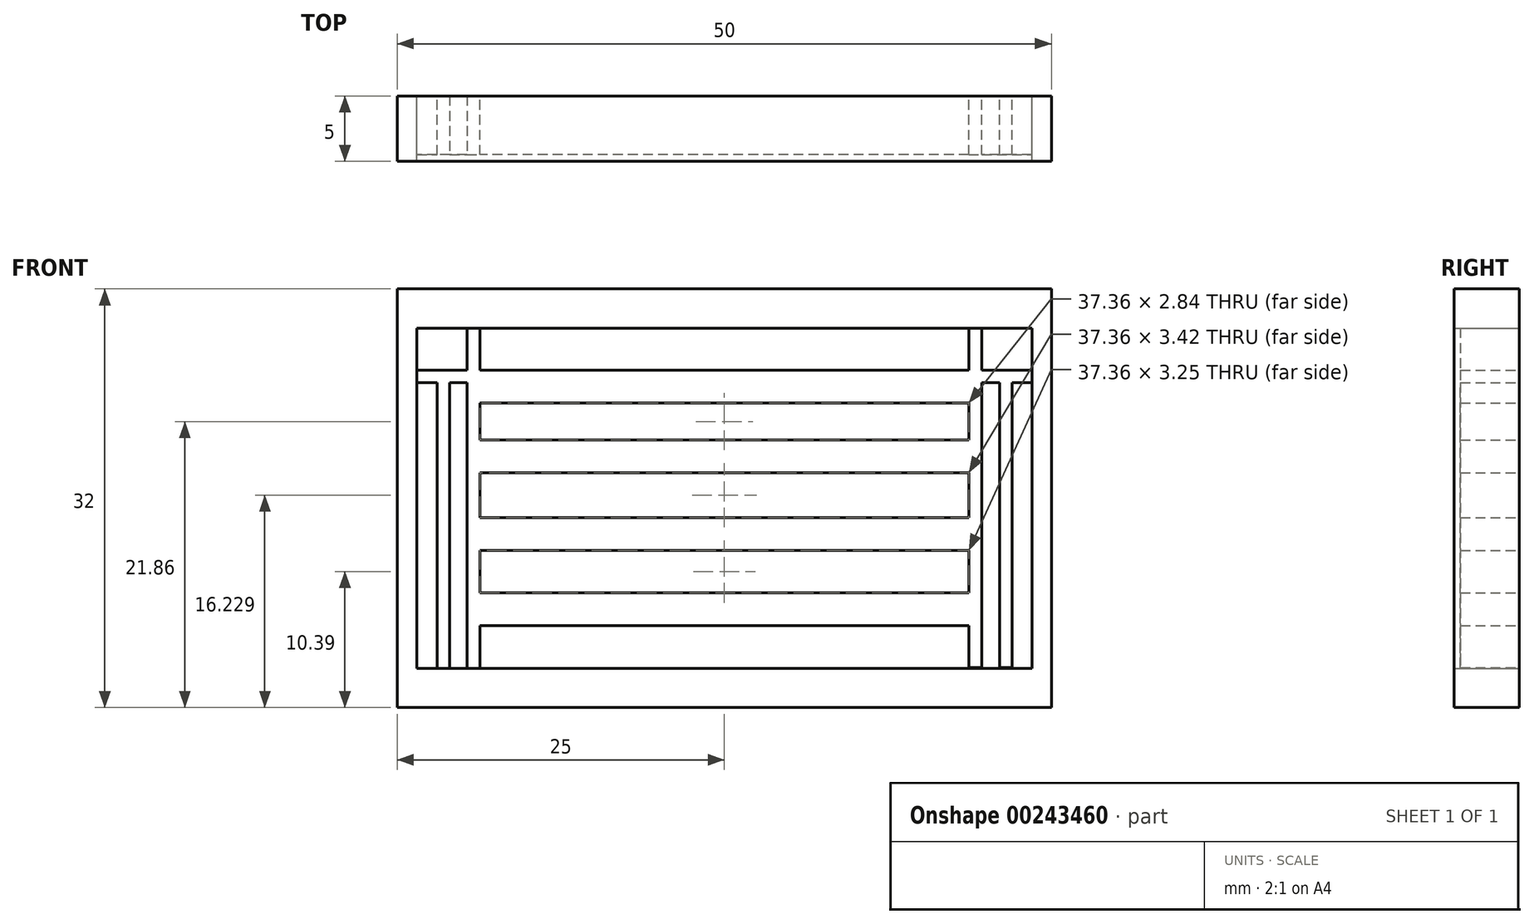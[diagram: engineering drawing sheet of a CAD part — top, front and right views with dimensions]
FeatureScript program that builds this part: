
annotation { "Feature Type Name" : "Feature", "Feature Type Description" : "" }
export const myFeature = defineFeature(function(context is Context, id is Id, definition is map)
    precondition{}
    {
        {
            var Q0;
            Q0=qCreatedBy(makeId("Front.planeOp"),FACE);
            var sketch = newSketch(context, id + "F0", { "sketchPlane" : qUnion([Q0])});
            skLineSegment(sketch, "E0", {"start": v(0, 0) * mm, "end": v(50, 0) * mm});
            skLineSegment(sketch, "E1", {"start": v(50, 0) * mm, "end": v(50, 32) * mm});
            skLineSegment(sketch, "E2", {"start": v(50, 32) * mm, "end": v(0, 32) * mm});
            skLineSegment(sketch, "E3", {"start": v(0, 32) * mm, "end": v(0, 0) * mm});
            skLineSegment(sketch, "E4", {"start": v(1.5, 29) * mm, "end": v(48.5, 29) * mm});
            skLineSegment(sketch, "E5", {"start": v(48.5, 29) * mm, "end": v(48.5, 3) * mm});
            skLineSegment(sketch, "E6", {"start": v(48.5, 3) * mm, "end": v(1.5, 3) * mm});
            skLineSegment(sketch, "E7", {"start": v(1.5, 3) * mm, "end": v(1.5, 29) * mm});
            skLineSegment(sketch, "E8", {"start": v(8, 29) * mm, "end": v(8, 3) * mm});
            skLineSegment(sketch, "E9", {"start": v(8, 3) * mm, "end": v(6.8, 3) * mm});
            skLineSegment(sketch, "E10", {"start": v(6.8, 3) * mm, "end": v(6.8, 29) * mm});
            skLineSegment(sketch, "E11", {"start": v(6.8, 29) * mm, "end": v(8, 29) * mm});
            skLineSegment(sketch, "E12", {"start": v(6.8, 26.52) * mm, "end": v(1.5, 26.52) * mm});
            skLineSegment(sketch, "E13", {"start": v(1.5, 26.52) * mm, "end": v(1.5, 25.4) * mm});
            skLineSegment(sketch, "E14", {"start": v(1.5, 25.4) * mm, "end": v(6.8, 25.4) * mm});
            skLineSegment(sketch, "E15", {"start": v(6.8, 25.4) * mm, "end": v(6.8, 26.52) * mm});
            skLineSegment(sketch, "E16", {"start": v(4.75, 25.4) * mm, "end": v(4.75, 3) * mm});
            skLineSegment(sketch, "E17", {"start": v(4.75, 3) * mm, "end": v(3.81, 3) * mm});
            skLineSegment(sketch, "E18", {"start": v(3.81, 3) * mm, "end": v(3.81, 25.4) * mm});
            skLineSegment(sketch, "E19", {"start": v(3.81, 25.4) * mm, "end": v(4.75, 25.4) * mm});
            skSolve(sketch);
        }
        {
            var Q0;
            Q0 = qSketchRegion(id + "F0", true);
            extrude(context, id + "F1", {"entities" : qUnion([Q0]), "depth" : 5 * mm, "offsetDistance" : 25 * mm});
        }
        {
            var Q0;
            Q0=qCreatedBy(makeId("Front.planeOp"),FACE);
            var sketch = newSketch(context, id + "F2", { "sketchPlane" : qUnion([Q0])});
            skLineSegment(sketch, "E20", {"start": v(6.32, 29.03) * mm, "end": v(6.32, 2.97) * mm});
            skLineSegment(sketch, "E21", {"start": v(6.32, 2.97) * mm, "end": v(5.32, 2.97) * mm});
            skLineSegment(sketch, "E22", {"start": v(5.32, 2.97) * mm, "end": v(5.32, 29.03) * mm});
            skLineSegment(sketch, "E23", {"start": v(5.32, 29.03) * mm, "end": v(6.32, 29.03) * mm});
            skLineSegment(sketch, "E24", {"start": v(5.32, 25.78) * mm, "end": v(1.5, 25.78) * mm});
            skLineSegment(sketch, "E25", {"start": v(1.5, 25.78) * mm, "end": v(1.5, 24.83) * mm});
            skLineSegment(sketch, "E26", {"start": v(1.5, 24.83) * mm, "end": v(5.32, 24.83) * mm});
            skLineSegment(sketch, "E27", {"start": v(5.32, 24.83) * mm, "end": v(5.32, 25.78) * mm});
            skLineSegment(sketch, "E28", {"start": v(4, 24.83) * mm, "end": v(4, 2.97) * mm});
            skLineSegment(sketch, "E29", {"start": v(4, 2.97) * mm, "end": v(3.05, 2.97) * mm});
            skLineSegment(sketch, "E30", {"start": v(3.05, 2.97) * mm, "end": v(3.05, 24.83) * mm});
            skLineSegment(sketch, "E31", {"start": v(3.05, 24.83) * mm, "end": v(4, 24.83) * mm});
            skLineSegment(sketch, "E32", {"start": v(43.5, 29) * mm, "end": v(44.68, 29) * mm});
            skLineSegment(sketch, "E33", {"start": v(44.68, 29) * mm, "end": v(44.68, 3.05) * mm});
            skLineSegment(sketch, "E34", {"start": v(44.68, 3.05) * mm, "end": v(43.68, 3.05) * mm});
            skLineSegment(sketch, "E35", {"start": v(43.68, 3.05) * mm, "end": v(43.68, 29) * mm});
            skLineSegment(sketch, "E36", {"start": v(44.68, 25.78) * mm, "end": v(48.5, 25.78) * mm});
            skLineSegment(sketch, "E37", {"start": v(48.5, 25.78) * mm, "end": v(48.5, 24.83) * mm});
            skLineSegment(sketch, "E38", {"start": v(48.5, 24.83) * mm, "end": v(46.98, 24.83) * mm});
            skLineSegment(sketch, "E39", {"start": v(44.68, 24.83) * mm, "end": v(44.68, 25.78) * mm});
            skPoint(sketch, "E40.end.orphan", {"position": v(46.59, 24.83) * mm});
            skPoint(sketch, "E40.start.orphan", {"position": v(46.98, 24.83) * mm});
            skPoint(sketch, "E41.start.orphan", {"position": v(47.01, 3.05) * mm});
            skLineSegment(sketch, "E42", {"start": v(46.98, 24.83) * mm, "end": v(46.98, 3.05) * mm});
            skLineSegment(sketch, "E43", {"start": v(46.98, 3.05) * mm, "end": v(46.03, 3.05) * mm});
            skLineSegment(sketch, "E44", {"start": v(46.03, 3.05) * mm, "end": v(46.03, 24.83) * mm});
            skLineSegment(sketch, "E45", {"start": v(46.03, 24.83) * mm, "end": v(46.98, 24.83) * mm});
            skLineSegment(sketch, "E46.trimOffspring", {"start": v(46.59, 24.83) * mm, "end": v(44.68, 24.83) * mm});
            skLineSegment(sketch, "E47", {"start": v(6.32, 25.78) * mm, "end": v(43.68, 25.78) * mm});
            skLineSegment(sketch, "E48", {"start": v(43.68, 25.78) * mm, "end": v(43.68, 23.28) * mm});
            skLineSegment(sketch, "E49", {"start": v(43.68, 23.28) * mm, "end": v(6.32, 23.28) * mm});
            skLineSegment(sketch, "E50", {"start": v(6.32, 23.28) * mm, "end": v(6.32, 25.78) * mm});
            skLineSegment(sketch, "E51", {"start": v(6.32, 20.44) * mm, "end": v(43.68, 20.44) * mm});
            skLineSegment(sketch, "E52", {"start": v(43.68, 20.44) * mm, "end": v(43.68, 17.94) * mm});
            skLineSegment(sketch, "E53", {"start": v(43.68, 17.94) * mm, "end": v(6.32, 17.94) * mm});
            skLineSegment(sketch, "E54", {"start": v(6.32, 17.94) * mm, "end": v(6.32, 20.44) * mm});
            skLineSegment(sketch, "E55", {"start": v(6.32, 14.52) * mm, "end": v(43.68, 14.52) * mm});
            skLineSegment(sketch, "E56", {"start": v(43.68, 14.52) * mm, "end": v(43.68, 12.02) * mm});
            skLineSegment(sketch, "E57", {"start": v(43.68, 12.02) * mm, "end": v(6.32, 12.02) * mm});
            skLineSegment(sketch, "E58", {"start": v(6.32, 12.02) * mm, "end": v(6.32, 14.52) * mm});
            skLineSegment(sketch, "E59", {"start": v(6.32, 8.76) * mm, "end": v(43.68, 8.76) * mm});
            skLineSegment(sketch, "E60", {"start": v(43.68, 8.76) * mm, "end": v(43.68, 6.26) * mm});
            skLineSegment(sketch, "E61", {"start": v(43.68, 6.26) * mm, "end": v(6.32, 6.26) * mm});
            skLineSegment(sketch, "E62", {"start": v(6.32, 6.26) * mm, "end": v(6.32, 8.76) * mm});
            skSolve(sketch);
        }
        {
            var Q0;
            Q0=makeQuery(id+"F2.imprint","IMPRINT",FACE,{"disambiguationData":[TD([[makeQuery(id+"F2.imprint","IMPRINT",EDGE,{"derivedFrom":sQuery(id+"F2.wireOp",EDGE,"E36")}),-1.0]])]});
            var Q1;
            Q1=makeQuery(id+"F2.imprint","IMPRINT",FACE,{"disambiguationData":[TD([[makeQuery(id+"F2.imprint","IMPRINT",EDGE,{"derivedFrom":sQuery(id+"F2.wireOp",EDGE,"E42")}),-1.0]])]});
            var Q2;
            {var subQ7=sQuery(id+"F2.wireOp",EDGE,"E34");Q2=makeQuery(id+"F2.imprint","IMPRINT",FACE,{"disambiguationData":[TD([[makeQuery(id+"F2.imprint","IMPRINT",EDGE,{"derivedFrom":subQ7}),-1.0]])]});}
            var Q3;
            Q3=makeQuery(id+"F2.imprint","IMPRINT",FACE,{"disambiguationData":[TD([[makeQuery(id+"F2.imprint","IMPRINT",EDGE,{"derivedFrom":sQuery(id+"F2.wireOp",EDGE,"E47")}),-1.0]])]});
            var Q4;
            Q4=makeQuery(id+"F2.imprint","IMPRINT",FACE,{"disambiguationData":[TD([[makeQuery(id+"F2.imprint","IMPRINT",EDGE,{"derivedFrom":sQuery(id+"F2.wireOp",EDGE,"E51")}),-1.0]])]});
            var Q5;
            Q5=makeQuery(id+"F2.imprint","IMPRINT",FACE,{"disambiguationData":[TD([[makeQuery(id+"F2.imprint","IMPRINT",EDGE,{"derivedFrom":sQuery(id+"F2.wireOp",EDGE,"E47")}),-1.0]])]});
            var Q6;
            Q6=makeQuery(id+"F2.imprint","IMPRINT",FACE,{"disambiguationData":[TD([[makeQuery(id+"F2.imprint","IMPRINT",EDGE,{"derivedFrom":sQuery(id+"F2.wireOp",EDGE,"E55")}),-1.0]])]});
            var Q7;
            Q7=makeQuery(id+"F2.imprint","IMPRINT",FACE,{"disambiguationData":[TD([[makeQuery(id+"F2.imprint","IMPRINT",EDGE,{"derivedFrom":sQuery(id+"F2.wireOp",EDGE,"E59")}),-1.0]])]});
            var Q8;
            {var subQ3=sQuery(id+"F2.wireOp",EDGE,"E21");Q8=makeQuery(id+"F2.imprint","IMPRINT",FACE,{"disambiguationData":[TD([[makeQuery(id+"F2.imprint","IMPRINT",EDGE,{"derivedFrom":subQ3}),-1.0]])]});}
            var Q9;
            Q9=makeQuery(id+"F2.imprint","IMPRINT",FACE,{"disambiguationData":[TD([[makeQuery(id+"F2.imprint","IMPRINT",EDGE,{"derivedFrom":sQuery(id+"F2.wireOp",EDGE,"E24")}),1.0]])]});
            var Q10;
            Q10=makeQuery(id+"F2.imprint","IMPRINT",FACE,{"disambiguationData":[TD([[makeQuery(id+"F2.imprint","IMPRINT",EDGE,{"derivedFrom":sQuery(id+"F2.wireOp",EDGE,"E28")}),-1.0]])]});
            extrude(context, id + "F3", {"entities" : qUnion([Q0, Q1, Q2, Q3, Q4, Q5, Q6, Q7, Q8, Q9, Q10]), "operationType" : NewBodyOperationType.ADD, "depth" : 4.5 * mm, "offsetDistance" : 25 * mm});
        }
    });
